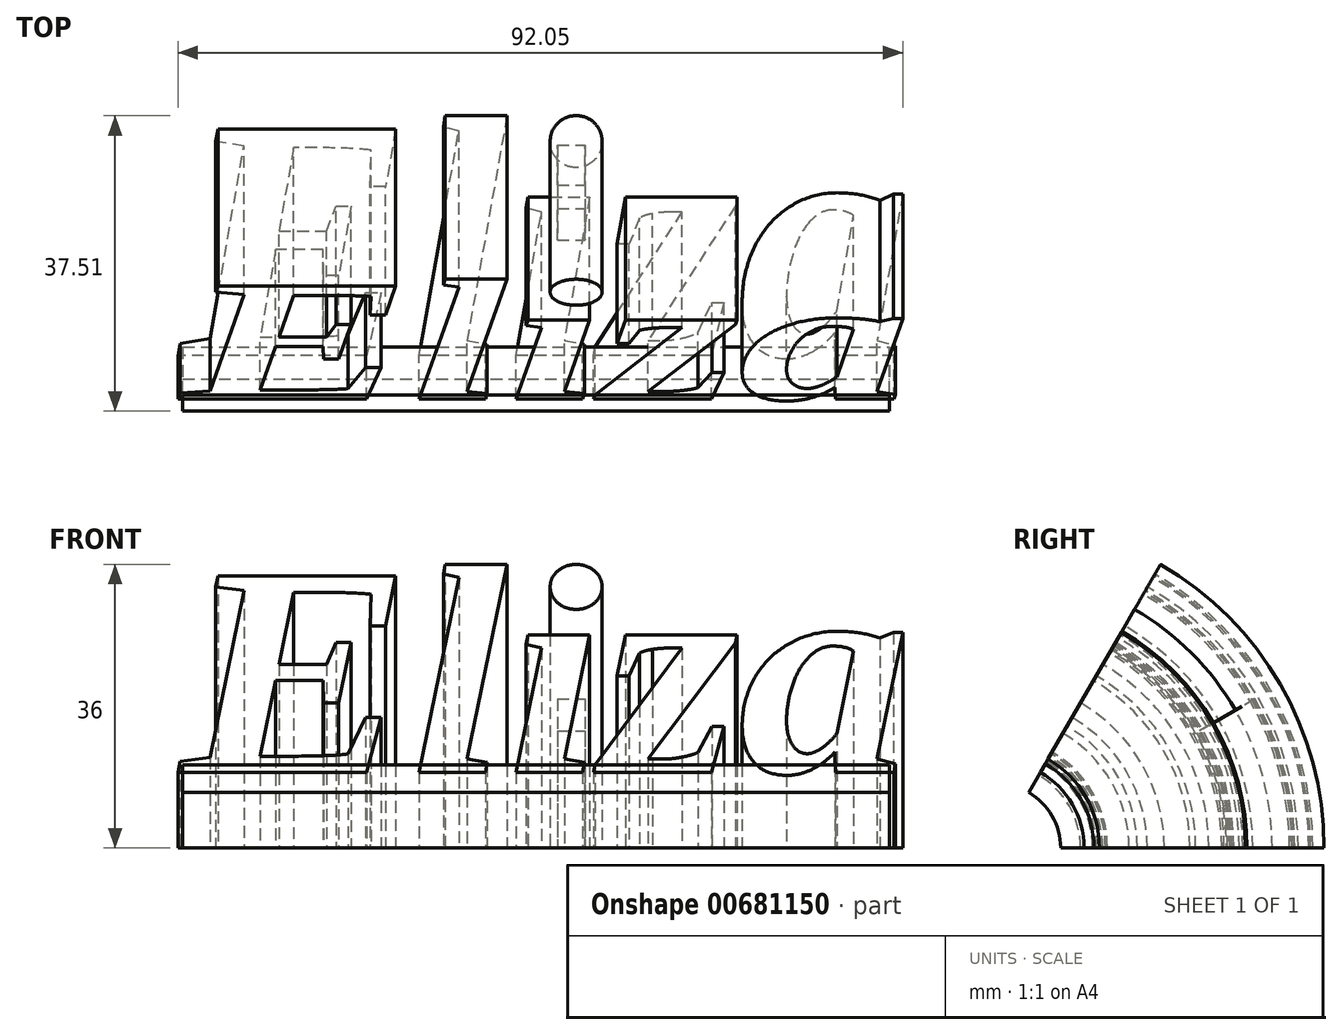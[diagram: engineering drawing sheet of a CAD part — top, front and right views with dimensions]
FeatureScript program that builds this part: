
annotation { "Feature Type Name" : "Feature", "Feature Type Description" : "" }
export const myFeature = defineFeature(function(context is Context, id is Id, definition is map)
    precondition{}
    {
        {
            var Q0;
            Q0=qCreatedBy(makeId("Top.planeOp"),FACE);
            var sketch = newSketch(context, id + "F0", { "sketchPlane" : qUnion([Q0])});
            skText(sketch, "E0", { "text": "Eliza", "fontName": "Tinos-BoldItalic.ttf"});
            const initialGuessF0  = {"E0": [-0.07616, -0.01534, 1, 0, 0.03163]};
            skSetInitialGuess(sketch, initialGuessF0);
            skSolve(sketch);
        }
        {
            var Q0;
            Q0=qCreatedBy(makeId("Top.planeOp"),FACE);
            var sketch = newSketch(context, id + "F1", { "sketchPlane" : qUnion([Q0])});
            skLineSegment(sketch, "E1.bottom", {"start": v(-75.89, -14.26) * mm, "end": v(13.85, -14.26) * mm});
            skLineSegment(sketch, "E1.top", {"start": v(-75.89, -18.31) * mm, "end": v(13.85, -18.31) * mm});
            skLineSegment(sketch, "E1.left", {"start": v(-75.89, -14.26) * mm, "end": v(-75.89, -18.31) * mm});
            skLineSegment(sketch, "E1.right", {"start": v(13.85, -14.26) * mm, "end": v(13.85, -18.31) * mm});
            skSolve(sketch);
        }
        {
            var Q0;
            Q0=qCreatedBy(makeId("Top.planeOp"),FACE);
            var sketch = newSketch(context, id + "F2", { "sketchPlane" : qUnion([Q0])});
            skLineSegment(sketch, "E2.bottom", {"start": v(-28.31, 11.42) * mm, "end": v(-24.8, 11.42) * mm});
            skLineSegment(sketch, "E2.top", {"start": v(-28.31, 3.31) * mm, "end": v(-24.8, 3.31) * mm});
            skLineSegment(sketch, "E2.left", {"start": v(-28.31, 11.42) * mm, "end": v(-28.31, 3.31) * mm});
            skLineSegment(sketch, "E2.right", {"start": v(-24.8, 11.42) * mm, "end": v(-24.8, 3.31) * mm});
            skSolve(sketch);
        }
        {
            var Q0;
            Q0=qCreatedBy(makeId("Top.planeOp"),FACE);
            var sketch = newSketch(context, id + "F3", { "sketchPlane" : qUnion([Q0])});
            skLineSegment(sketch, "E3", {"start": v(-81.02, -26.42) * mm, "end": v(35.75, -26.42) * mm});
            skSolve(sketch);
        }
        {
            var Q0;
            Q0=makeQuery(id+"F1.imprint","IMPRINT",FACE,{"disambiguationData":[TD([[makeQuery(id+"F1.imprint","IMPRINT",EDGE,{"derivedFrom":sQuery(id+"F1.wireOp",EDGE,"E1.bottom")}),-1.0]])]});
            var Q1;
            Q1 = qSketchRegion(id + "F0", true);
            var Q2;
            Q2=sQuery(id+"F3.wireOp",EDGE,"E3");
            revolve(context, id + "F4", {"entities" : qUnion([Q0, Q1]), "axis" : qUnion([Q2]), "revolveType" : RevolveType.ONE_DIRECTION, "angle" : 60 * degree});
        }
        {
            var Q0;
            Q0 = qSketchRegion(id + "F2", true);
            var Q1;
            Q1=sQuery(id+"F3.wireOp",EDGE,"E3");
            revolve(context, id + "F5", {"entities" : qUnion([Q0]), "axis" : qUnion([Q1]), "revolveType" : RevolveType.ONE_DIRECTION, "angle" : 30 * degree});
        }
    });
